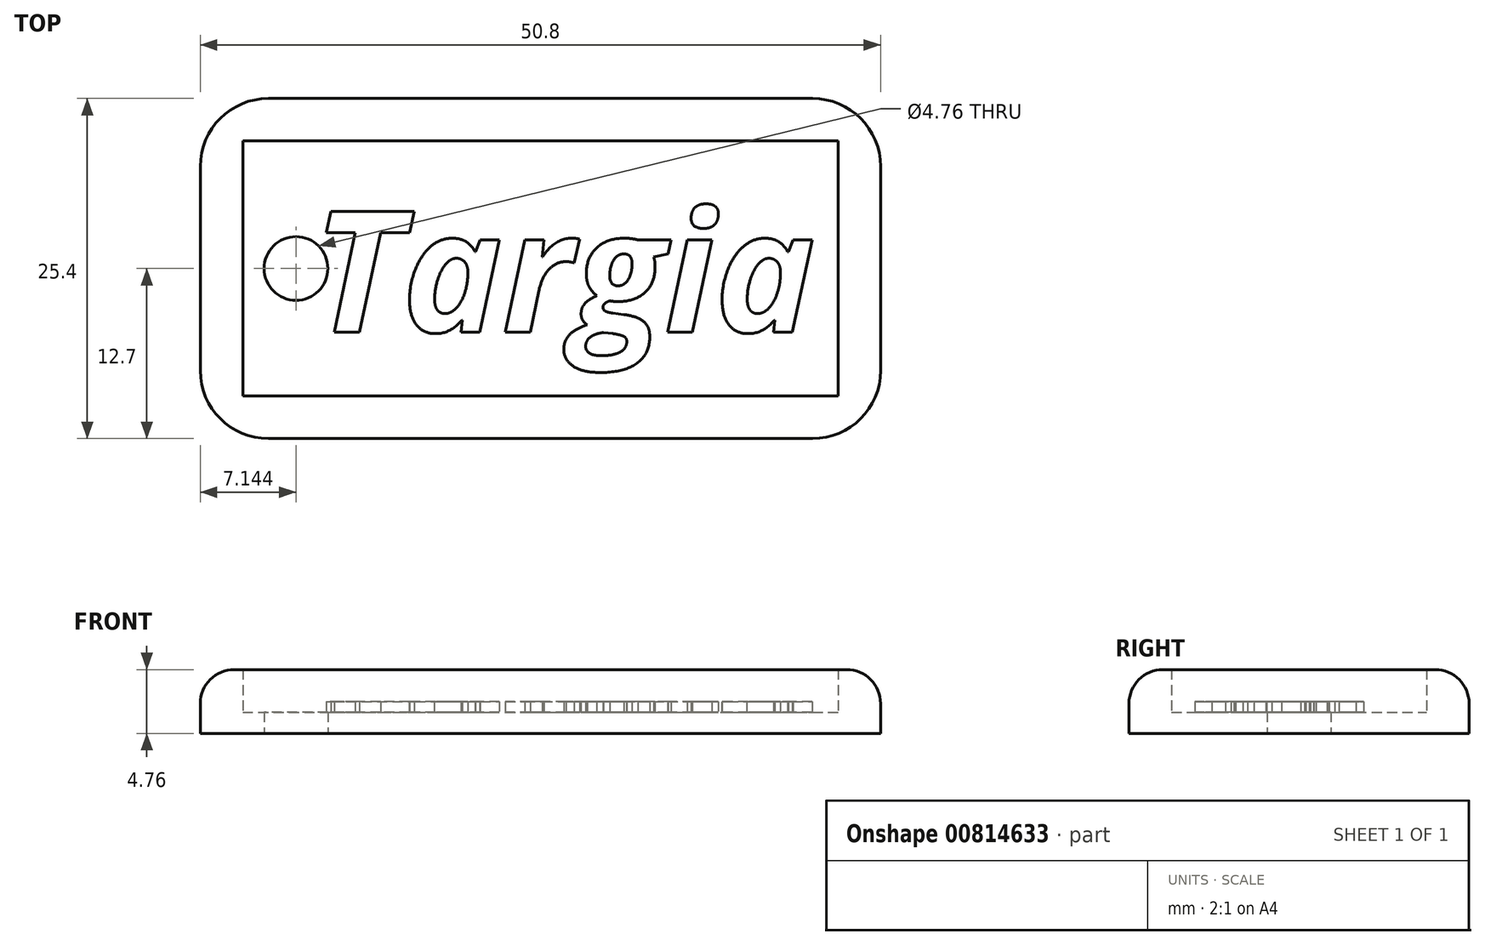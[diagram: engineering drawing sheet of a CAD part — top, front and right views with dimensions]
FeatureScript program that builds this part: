
annotation { "Feature Type Name" : "Feature", "Feature Type Description" : "" }
export const myFeature = defineFeature(function(context is Context, id is Id, definition is map)
    precondition{}
    {
        {
            var Q0;
            Q0=qCreatedBy(makeId("Top.planeOp"),FACE);
            var sketch = newSketch(context, id + "F0", { "sketchPlane" : qUnion([Q0])});
            skLineSegment(sketch, "E0.bottom", {"start": v(0, 0) * mm, "end": v(50.8, 0) * mm});
            skLineSegment(sketch, "E0.top", {"start": v(0, 25.4) * mm, "end": v(50.8, 25.4) * mm});
            skLineSegment(sketch, "E0.left", {"start": v(0, 0) * mm, "end": v(0, 25.4) * mm});
            skLineSegment(sketch, "E0.right", {"start": v(50.8, 0) * mm, "end": v(50.8, 25.4) * mm});
            skCircle(sketch, "E1", {"center": v(7.14, 12.7) * mm, "radius": 2.38 * mm});
            skPoint(sketch, "E1.centerSnap0", {"position": v(0, 12.7) * mm});
            skLineSegment(sketch, "E2.0", {"start": v(3.17, 22.23) * mm, "end": v(47.62, 22.23) * mm});
            skLineSegment(sketch, "E2.1", {"start": v(3.18, 3.18) * mm, "end": v(3.17, 22.22) * mm});
            skLineSegment(sketch, "E2.2", {"start": v(3.18, 3.18) * mm, "end": v(47.62, 3.18) * mm});
            skLineSegment(sketch, "E2.3", {"start": v(47.62, 3.18) * mm, "end": v(47.62, 22.23) * mm});
            skSolve(sketch);
        }
        {
            var Q0;
            Q0=makeQuery(id+"F0.imprint","IMPRINT",FACE,{"disambiguationData":[TD([[makeQuery(id+"F0.imprint","IMPRINT",EDGE,{"derivedFrom":sQuery(id+"F0.wireOp",EDGE,"E1")}),-1.0]])]});
            extrude(context, id + "F1", {"entities" : qUnion([Q0]), "depth" : 1.59 * mm, "offsetDistance" : 25.4 * mm});
        }
        {
            var Q0;
            Q0 = qSketchRegion(id + "F0", true);
            extrude(context, id + "F2", {"entities" : qUnion([Q0]), "operationType" : NewBodyOperationType.ADD, "depth" : 4.76 * mm, "offsetDistance" : 25.4 * mm});
        }
        {
            var Q0;
            Q0=makeQuery(id+"F2.opExtrude","SWEPT_EDGE",EDGE,{"disambiguationData":[OSD([sQuery(id+"F0.wireOp",EDGE,"E0.bottom"),sQuery(id+"F0.wireOp",EDGE,"E0.right")])]});
            var Q1;
            Q1=makeQuery(id+"F2.opExtrude","SWEPT_EDGE",EDGE,{"disambiguationData":[OSD([sQuery(id+"F0.wireOp",EDGE,"E0.bottom"),sQuery(id+"F0.wireOp",EDGE,"E0.left")])]});
            var Q2;
            Q2=makeQuery(id+"F2.opExtrude","SWEPT_EDGE",EDGE,{"disambiguationData":[OSD([sQuery(id+"F0.wireOp",EDGE,"E0.top"),sQuery(id+"F0.wireOp",EDGE,"E0.right")])]});
            var Q3;
            Q3=makeQuery(id+"F2.opExtrude","SWEPT_EDGE",EDGE,{"disambiguationData":[OSD([sQuery(id+"F0.wireOp",EDGE,"E0.top"),sQuery(id+"F0.wireOp",EDGE,"E0.left")])]});
            fillet(context, id + "F3", {"entities" : qUnion([Q0, Q1, Q2, Q3]), "radius" : 5.08 * mm, "tangentPropagation" : true, "allowEdgeOverflow" : false});
        }
        {
            var Q0;
            Q0=makeQuery(id+"F2.opExtrude","CAP_EDGE",EDGE,{"disambiguationData":[OSD([sQuery(id+"F0.wireOp",EDGE,"E0.bottom")])],"isStart":false});
            fillet(context, id + "F4", {"entities" : qUnion([Q0]), "radius" : 2.54 * mm, "tangentPropagation" : true, "allowEdgeOverflow" : false});
        }
        {
            var Q0;
            Q0=makeQuery(id+"F1.opExtrude","CAP_FACE",FACE,{"disambiguationData":[OSD([sQuery(id+"F0.wireOp",EDGE,"E1"),sQuery(id+"F0.wireOp",EDGE,"E2.0"),sQuery(id+"F0.wireOp",EDGE,"E2.1"),sQuery(id+"F0.wireOp",EDGE,"E2.2"),sQuery(id+"F0.wireOp",EDGE,"E2.3")])],"isStart":false});
            var sketch = newSketch(context, id + "F5", { "sketchPlane" : qUnion([Q0])});
            skText(sketch, "E3", { "text": "Targia", "fontName": "OpenSans-BoldItalic.ttf"});
            const initialGuessF5  = {"E3": [0.00838, 0.00796, 1, 0, 0.00907]};
            skSetInitialGuess(sketch, initialGuessF5);
            skSolve(sketch);
        }
        {
            var Q0;
            Q0 = qSketchRegion(id + "F5", true);
            extrude(context, id + "F6", {"entities" : qUnion([Q0]), "operationType" : NewBodyOperationType.ADD, "depth" : 0.8 * mm, "offsetDistance" : 25.4 * mm});
        }
    });
